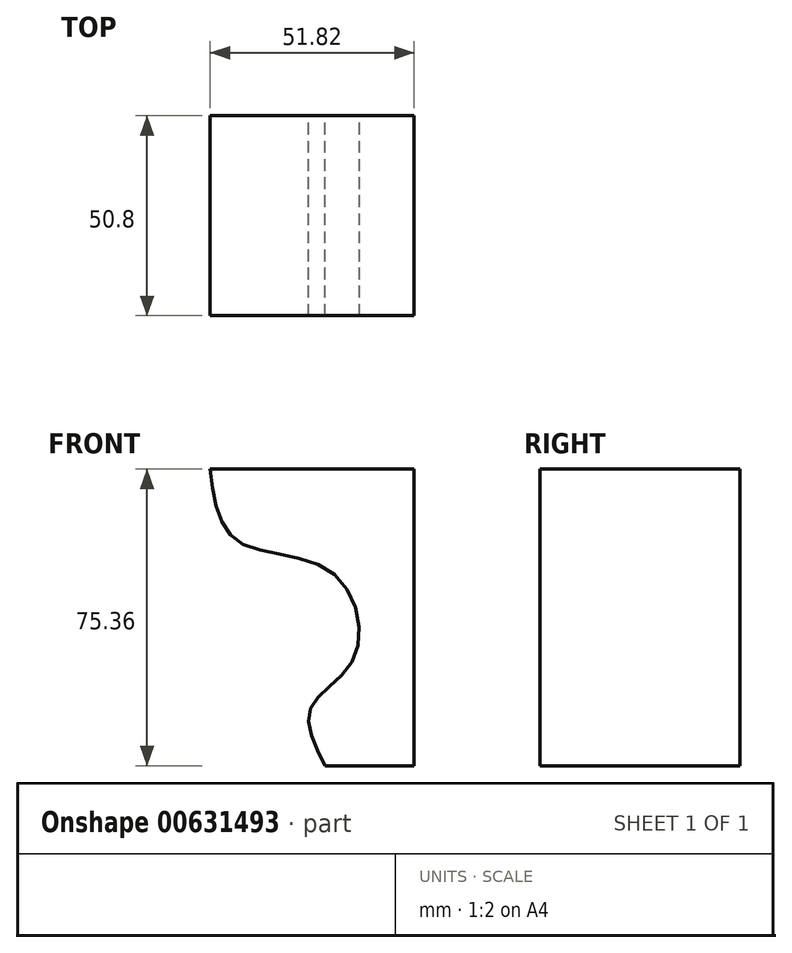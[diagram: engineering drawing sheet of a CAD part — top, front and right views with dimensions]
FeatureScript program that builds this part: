
annotation { "Feature Type Name" : "Feature", "Feature Type Description" : "" }
export const myFeature = defineFeature(function(context is Context, id is Id, definition is map)
    precondition{}
    {
        {
            var Q0;
            Q0=qCreatedBy(makeId("Front.planeOp"),FACE);
            var sketch = newSketch(context, id + "F0", { "sketchPlane" : qUnion([Q0])});
            skLineSegment(sketch, "E0.bottom", {"start": v(29.4, 37.68) * mm, "end": v(-29.4, 37.68) * mm});
            skLineSegment(sketch, "E0.top", {"start": v(29.4, -37.68) * mm, "end": v(-29.4, -37.68) * mm});
            skLineSegment(sketch, "E0.left", {"start": v(29.4, 37.68) * mm, "end": v(29.4, -37.68) * mm});
            skLineSegment(sketch, "E0.right", {"start": v(-29.4, 37.68) * mm, "end": v(-29.4, -37.68) * mm});
            skPoint(sketch, "E0.middle", {"position": v(0, 0) * mm});
            skFitSpline(sketch, "E1", {"points": [v(-22.4, 37.68) * mm, v(-15.5, 19.4) * mm, v(8.27, 11.58) * mm, v(14.29, -10.08) * mm, v(3.16, -23.01) * mm, v(6.77, -37.68) * mm], "startDerivative": vector(13.58, -111.52) * mm, "endDerivative": vector(45.5, -90.88) * mm});
            skSolve(sketch);
        }
        {
            var Q0;
            {var subQ0=sQuery(id+"F0.wireOp",EDGE,"E0.left");Q0=makeQuery(id+"F0.imprint","IMPRINT",FACE,{"disambiguationData":[TD([[makeQuery(id+"F0.imprint","IMPRINT",EDGE,{"derivedFrom":subQ0}),-1.0]])]});}
            extrude(context, id + "F1", {"entities" : qUnion([Q0]), "depth" : 50.8 * mm, "offsetDistance" : 25.4 * mm});
        }
    });
